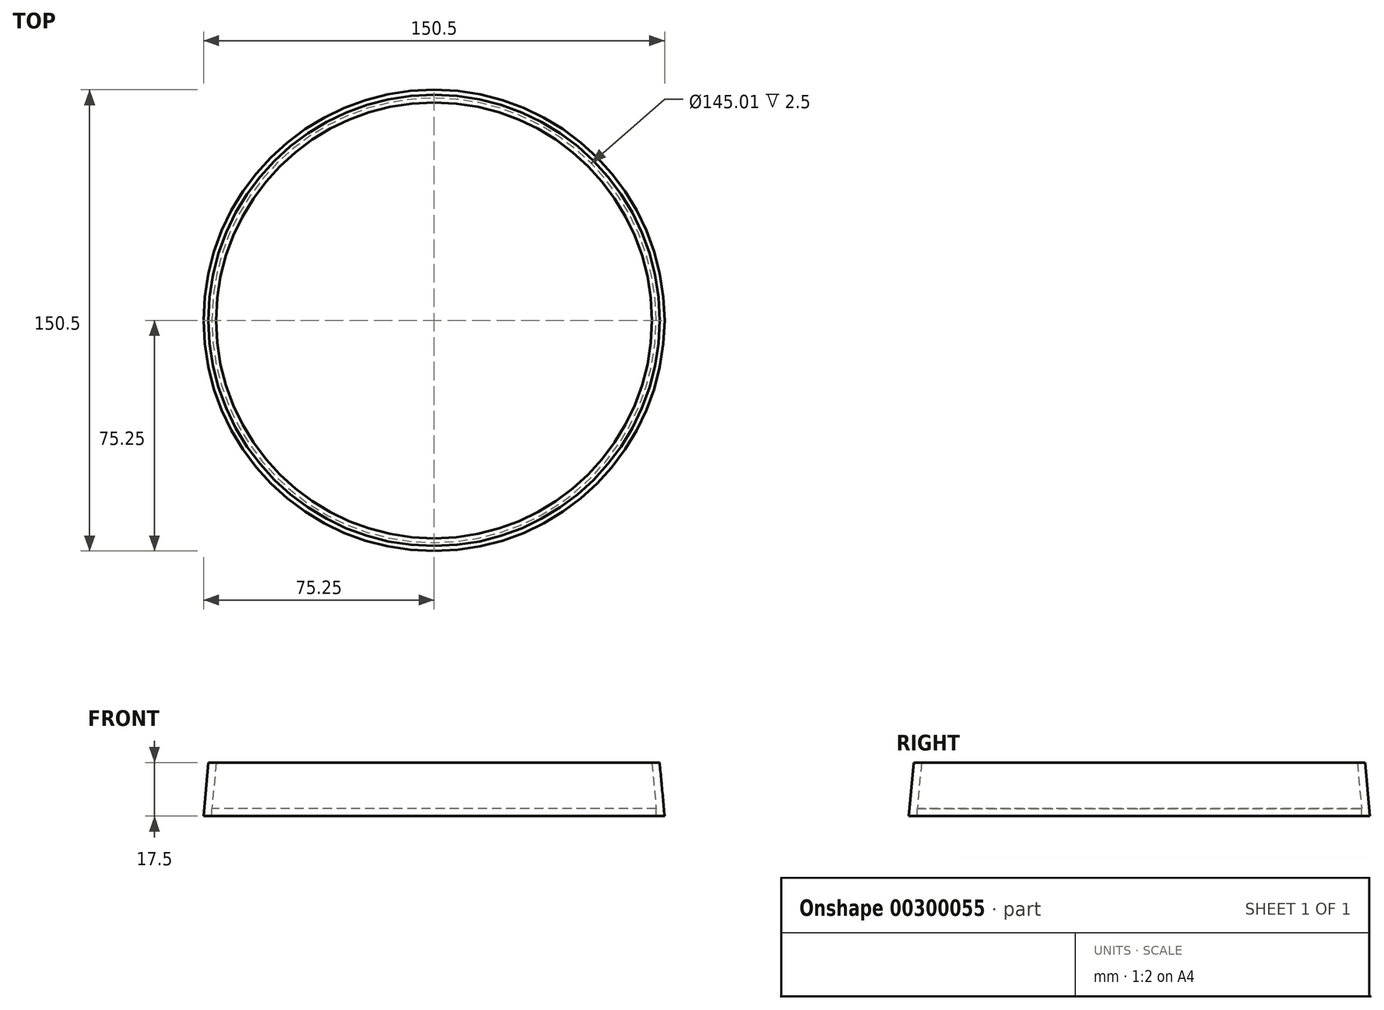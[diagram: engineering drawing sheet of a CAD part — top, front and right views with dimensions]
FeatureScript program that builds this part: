
annotation { "Feature Type Name" : "Feature", "Feature Type Description" : "" }
export const myFeature = defineFeature(function(context is Context, id is Id, definition is map)
    precondition{}
    {
        {
            assignVariable(context, id + "F0", {"name" : "bucket_t", "anyValue" : 0.75});
        }
        {
            assignVariable(context, id + "F1", {"name" : "bucket_top_d", "anyValue" : 165 - (getVariable(context, 'bucket_t') * 2)});
        }
        {
            assignVariable(context, id + "F2", {"name" : "bucket_bot_d", "anyValue" : 139 - (getVariable(context, 'bucket_t') * 2)});
        }
        {
            assignVariable(context, id + "F3", {"name" : "bucket_h", "anyValue" : 140});
        }
        {
            assignVariable(context, id + "F4", {"name" : "bucket_angle", "anyValue" : atan(((getVariable(context, 'bucket_top_d') - getVariable(context, 'bucket_bot_d')) / 2) / getVariable(context, 'bucket_h'))});
        }
        {
            assignVariable(context, id + "F5", {"name" : "screen_h", "anyValue" : 2.5});
        }
        {
            assignVariable(context, id + "F6", {"name" : "rim_h", "anyValue" : 15});
        }
        {
            assignVariable(context, id + "F7", {"name" : "spacer_h", "anyValue" : getVariable(context, 'screen_h') + getVariable(context, 'rim_h')});
        }
        {
            var Q0;
            Q0=qCreatedBy(makeId("Top.planeOp"),FACE);
            var sketch = newSketch(context, id + "F8", { "sketchPlane" : qUnion([Q0])});
            skCircle(sketch, "E0", {"center": v(0, 0) * mm, "radius": 75.25 * mm});
            skSolve(sketch);
        }
        {
            var Q0;
            Q0=makeQuery(id+"F8.imprint","IMPRINT",FACE,{"disambiguationData":[TD([[makeQuery(id+"F8.imprint","IMPRINT",EDGE,{"derivedFrom":sQuery(id+"F8.wireOp",EDGE,"E0")}),1.0]])]});
            extrude(context, id + "F9", {"entities" : qUnion([Q0]), "depth" : (getVariable(context, 'spacer_h')) * mm, "hasDraft" : true, "draftAngle" : getVariable(context, 'bucket_angle'), "draftPullDirection" : true});
        }
        {
            var Q0;
            Q0=makeQuery(id+"F9.opExtrude","CAP_FACE",FACE,{"disambiguationData":[OSD([sQuery(id+"F8.wireOp",EDGE,"E0")])],"isStart":false});
            shell(context, id + "F10", {"entities" : qUnion([Q0]), "thickness" : (getVariable(context, 'screen_h')) * mm});
        }
        {
            var Q0;
            {var subQ0=sQuery(id+"F8.wireOp",EDGE,"E0");Q0=makeQuery(id+"F10.opShell","OFFSET_FACE",FACE,{"disambiguationData":[OSD([subQ0]),TDD([makeQuery(id+"F9.opExtrude","CAP_FACE",FACE,{"disambiguationData":[OSD([subQ0])],"isStart":true})])]});}
            var sketch = newSketch(context, id + "F11", { "sketchPlane" : qUnion([Q0])});
            skCircle(sketch, "E1.0.0", {"center": v(0, 0) * mm, "radius": 72.5 * mm});
            skSolve(sketch);
        }
        {
            var Q0;
            Q0=qSketchRegion(id+"F11",true);
            var Q1;
            Q1=makeQuery(id+"F9.opExtrude","CAP_FACE",FACE,{"disambiguationData":[OSD([sQuery(id+"F8.wireOp",EDGE,"E0")])],"isStart":true});
            extrude(context, id + "F12", {"entities" : qUnion([Q0]), "operationType" : NewBodyOperationType.REMOVE, "endBound" : BoundingType.UP_TO_SURFACE, "oppositeDirection" : true, "endBoundEntityFace" : qUnion([Q1]), "depth" : 25 * mm});
        }
        {
            var Q0;
            Q0=qSketchRegion(id+"F11",true);
            var Q1;
            Q1=makeQuery(id+"F9.opExtrude","CAP_FACE",FACE,{"disambiguationData":[OSD([sQuery(id+"F8.wireOp",EDGE,"E0")])],"isStart":true});
            extrude(context, id + "F13", {"entities" : qUnion([Q0]), "endBound" : BoundingType.UP_TO_SURFACE, "oppositeDirection" : true, "endBoundEntityFace" : qUnion([Q1]), "depth" : 25 * mm});
        }
    });
